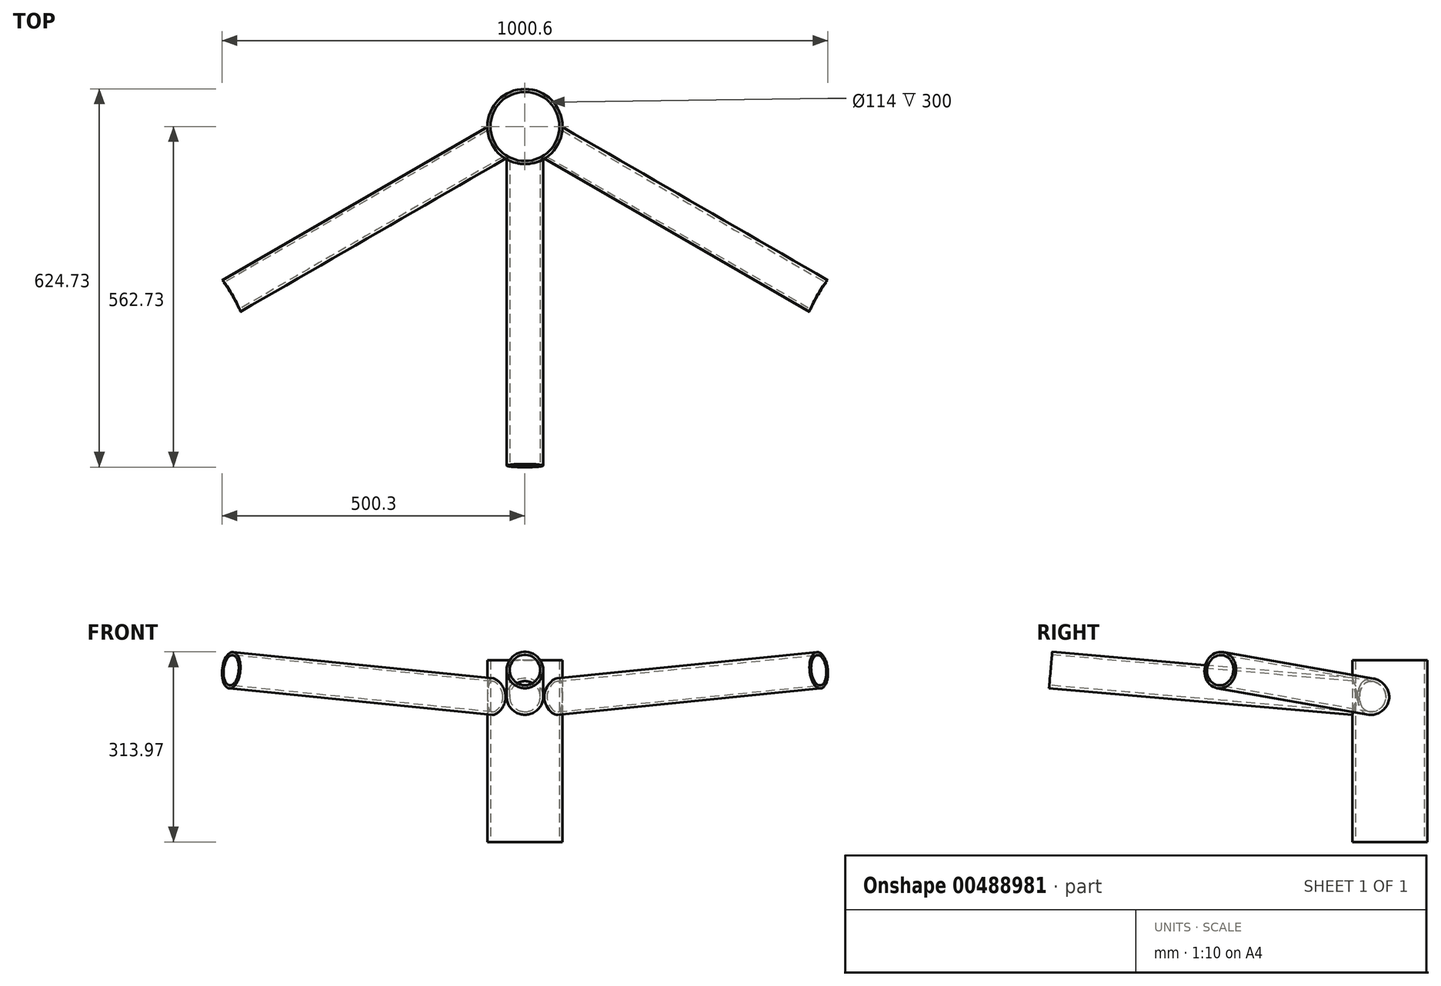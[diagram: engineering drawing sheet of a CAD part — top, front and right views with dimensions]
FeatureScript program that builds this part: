
annotation { "Feature Type Name" : "Feature", "Feature Type Description" : "" }
export const myFeature = defineFeature(function(context is Context, id is Id, definition is map)
    precondition{}
    {
        {
            var Q0;
            Q0=qCreatedBy(makeId("Top.planeOp"),FACE);
            var sketch = newSketch(context, id + "F0", { "sketchPlane" : qUnion([Q0])});
            skCircle(sketch, "E0", {"center": v(0, 0) * mm, "radius": 57 * mm});
            skCircle(sketch, "E1", {"center": v(0, 0) * mm, "radius": 62 * mm});
            skSolve(sketch);
        }
        {
            var Q0;
            Q0 = qSketchRegion(id + "F0", true);
            extrude(context, id + "F1", {"entities" : qUnion([Q0]), "depth" : 300 * mm});
        }
        {
            var Q0;
            Q0=qCreatedBy(makeId("Top.planeOp"),FACE);
            cPlane(context, id + "F2", {"entities" : qUnion([Q0]), "cplaneType" : CPlaneType.OFFSET, "offset" : 240 * mm, "width" : 152.4 * mm, "height" : 152.4 * mm});
        }
        {
            var Q0;
            Q0=qCreatedBy(makeId("Right.planeOp"),FACE);
            var sketch = newSketch(context, id + "F3", { "sketchPlane" : qUnion([Q0])});
            skLineSegment(sketch, "E2", {"start": v(-62, 0.35) * mm, "end": v(-62, 300) * mm});
            skLineSegment(sketch, "E3", {"start": v(62, 300) * mm, "end": v(62, 0) * mm});
            skLineSegment(sketch, "E4", {"start": v(-62, 240.35) * mm, "end": v(-560.1, 283.93) * mm});
            skSolve(sketch);
        }
        {
            var Q0;
            Q0=sQuery(id+"F3.wireOp",VERTEX,"E4.end");
            var Q1;
            Q1=sQuery(id+"F3.wireOp",EDGE,"E4");
            cPlane(context, id + "F4", {"entities" : qUnion([Q0, Q1]), "cplaneType" : CPlaneType.LINE_POINT, "offset" : 25.4 * mm, "width" : 152.4 * mm, "height" : 152.4 * mm});
        }
        {
            var Q0;
            Q0=qCreatedBy(id+"F4.planeOp",FACE);
            var sketch = newSketch(context, id + "F5", { "sketchPlane" : qUnion([Q0])});
            skPoint(sketch, "E5.0", {"position": v(0, 234.04) * mm});
            skCircle(sketch, "E6", {"center": v(0, 234.04) * mm, "radius": 30.15 * mm});
            skCircle(sketch, "E7", {"center": v(0, 234.04) * mm, "radius": 25.15 * mm});
            skSolve(sketch);
        }
        {
            var Q0;
            Q0 = qSketchRegion(id + "F5", true);
            var Q1;
            Q1=makeQuery(id+"F1.opExtrude","SWEPT_FACE",FACE,{"disambiguationData":[OSD([sQuery(id+"F0.wireOp",EDGE,"E1")])]});
            extrude(context, id + "F6", {"entities" : qUnion([Q0]), "endBound" : BoundingType.UP_TO_SURFACE, "oppositeDirection" : true, "endBoundEntityFace" : qUnion([Q1]), "depth" : 25.4 * mm});
        }
        {
            var Q0;
            Q0=qCreatedBy(id+"F2.planeOp",FACE);
            var sketch = newSketch(context, id + "F7", { "sketchPlane" : qUnion([Q0])});
            skLineSegment(sketch, "E8", {"start": v(0, 0) * mm, "end": v(433.01, -250) * mm, "construction": true});
            skLineSegment(sketch, "E9", {"start": v(0, 0) * mm, "end": v(-433.01, -250) * mm, "construction": true});
            skSolve(sketch);
        }
        {
            var Q0;
            Q0=sQuery(id+"F7.wireOp",EDGE,"E9");
            var Q1;
            Q1=qCreatedBy(makeId("Right.planeOp"),FACE);
            cPlane(context, id + "F8", {"entities" : qUnion([Q0, Q1]), "cplaneType" : CPlaneType.LINE_ANGLE, "offset" : 0 * mm, "angle" : 0 * degree, "width" : 152.4 * mm, "height" : 152.4 * mm});
        }
        {
            var Q0;
            Q0=qCreatedBy(id+"F8.planeOp",FACE);
            var sketch = newSketch(context, id + "F9", { "sketchPlane" : qUnion([Q0])});
            skLineSegment(sketch, "E10", {"start": v(62, 300) * mm, "end": v(62, 0) * mm});
            skLineSegment(sketch, "E11.0", {"start": v(0, 240) * mm, "end": v(500, 240) * mm});
            skLineSegment(sketch, "E12", {"start": v(62, 240) * mm, "end": v(560.1, 283.58) * mm});
            skSolve(sketch);
        }
        {
            var Q0;
            Q0=sQuery(id+"F9.wireOp",EDGE,"E12");
            var Q1;
            Q1=sQuery(id+"F9.wireOp",VERTEX,"E12.end");
            cPlane(context, id + "F10", {"entities" : qUnion([Q0, Q1]), "cplaneType" : CPlaneType.LINE_POINT, "offset" : 25.4 * mm, "width" : 152.4 * mm, "height" : 152.4 * mm});
        }
        {
            var Q0;
            Q0=qCreatedBy(id+"F10.planeOp",FACE);
            var sketch = newSketch(context, id + "F11", { "sketchPlane" : qUnion([Q0])});
            skPoint(sketch, "E13.0", {"position": v(-11.74, 233.39) * mm});
            skCircle(sketch, "E14", {"center": v(-11.74, 233.39) * mm, "radius": 25.15 * mm});
            skCircle(sketch, "E15", {"center": v(-11.74, 233.39) * mm, "radius": 30.15 * mm});
            skSolve(sketch);
        }
        {
            var Q0;
            Q0 = qSketchRegion(id + "F11", true);
            var Q1;
            Q1=makeQuery(id+"F1.opExtrude","SWEPT_FACE",FACE,{"disambiguationData":[OSD([sQuery(id+"F0.wireOp",EDGE,"E1")])]});
            extrude(context, id + "F12", {"entities" : qUnion([Q0]), "endBound" : BoundingType.UP_TO_SURFACE, "oppositeDirection" : true, "endBoundEntityFace" : qUnion([Q1]), "depth" : 25.4 * mm});
        }
        {
            var Q0;
            Q0=makeQuery(id+"F12.opExtrude","SWEPT_BODY",BODY,{"disambiguationData":[OSD([sQuery(id+"F11.wireOp",EDGE,"E14"),sQuery(id+"F11.wireOp",EDGE,"E15")])]});
            var Q1;
            Q1=makeQuery(id+"F1.opExtrude","SWEPT_FACE",FACE,{"disambiguationData":[OSD([sQuery(id+"F0.wireOp",EDGE,"E0")])]});
            circularPattern(context, id + "F13", {"entities" : qUnion([Q0]), "axis" : qUnion([Q1]), "angle" : 120 * degree, "instanceCount" : 2, "equalSpace" : true});
        }
    });
